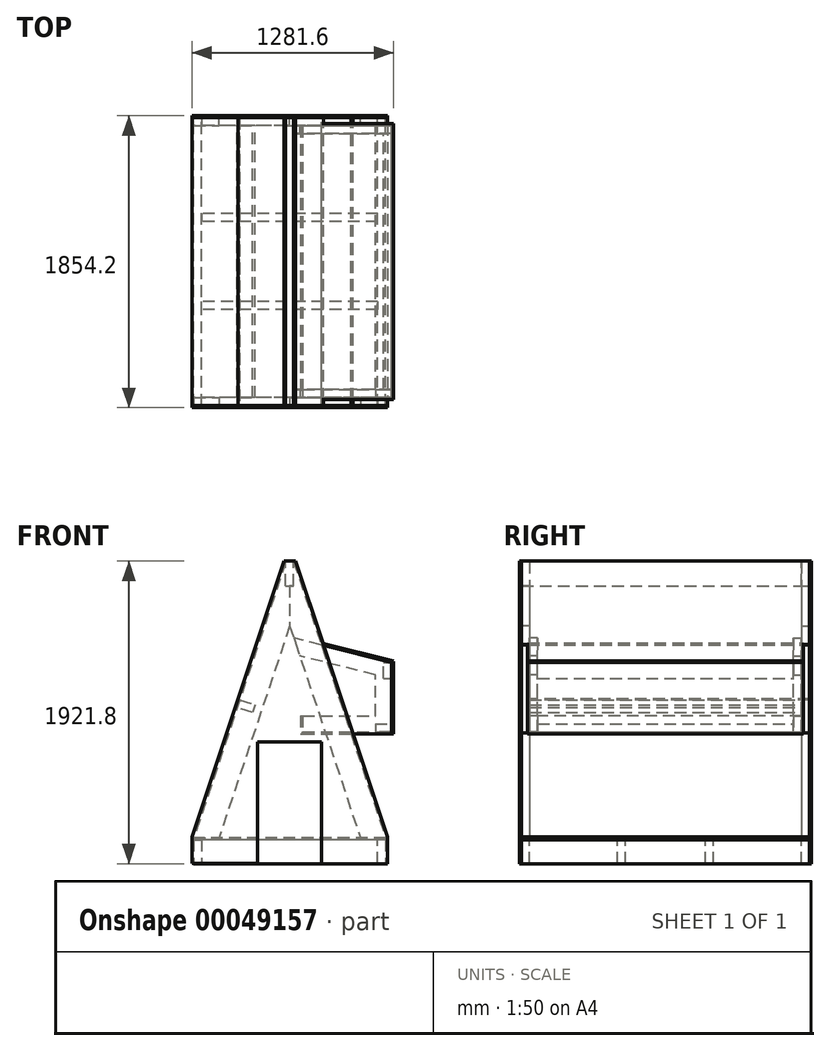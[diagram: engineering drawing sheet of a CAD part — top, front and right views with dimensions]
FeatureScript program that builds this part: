
annotation { "Feature Type Name" : "Feature", "Feature Type Description" : "" }
export const myFeature = defineFeature(function(context is Context, id is Id, definition is map)
    precondition{}
    {
        {
            var Q0;
            Q0=qCreatedBy(makeId("Top.planeOp"),FACE);
            var sketch = newSketch(context, id + "F0", { "sketchPlane" : qUnion([Q0])});
            skLineSegment(sketch, "E0.rect.bottom", {"start": v(609.6, 914.4) * mm, "end": v(-609.6, 914.4) * mm});
            skLineSegment(sketch, "E0.rect.top", {"start": v(609.6, -914.4) * mm, "end": v(-609.6, -914.4) * mm});
            skLineSegment(sketch, "E0.rect.left", {"start": v(609.6, 914.4) * mm, "end": v(609.6, -914.4) * mm});
            skLineSegment(sketch, "E0.rect.right", {"start": v(-609.6, 914.4) * mm, "end": v(-609.6, -914.4) * mm});
            skPoint(sketch, "E0.rect.middle", {"position": v(0, 0) * mm});
            skSolve(sketch);
        }
        {
            var Q0;
            Q0=qCreatedBy(makeId("Front.planeOp"),FACE);
            var sketch = newSketch(context, id + "F1", { "sketchPlane" : qUnion([Q0])});
            skLineSegment(sketch, "E1.bottom", {"start": v(-609.6, 0) * mm, "end": v(-558.8, 0) * mm});
            skLineSegment(sketch, "E1.top", {"start": v(-609.6, -152.4) * mm, "end": v(-558.8, -152.4) * mm});
            skLineSegment(sketch, "E1.left", {"start": v(-609.6, 0) * mm, "end": v(-609.6, -152.4) * mm});
            skLineSegment(sketch, "E1.right", {"start": v(-558.8, 0) * mm, "end": v(-558.8, -152.4) * mm});
            skSolve(sketch);
        }
        {
            var Q0;
            Q0=makeQuery(id+"F1.imprint","IMPRINT",FACE,{"disambiguationData":[TD([[makeQuery(id+"F1.imprint","IMPRINT",EDGE,{"derivedFrom":sQuery(id+"F1.wireOp",EDGE,"E1.bottom")}),-1.0]])]});
            extrude(context, id + "F2", {"entities" : qUnion([Q0]), "depth" : 914.4 * mm, "hasSecondDirection" : true, "secondDirectionOppositeDirection" : true, "secondDirectionDepth" : 914.4 * mm});
        }
        {
            var Q0;
            Q0=makeQuery(id+"F2.opExtrude","SWEPT_BODY",BODY,{"disambiguationData":[OSD([sQuery(id+"F1.wireOp",EDGE,"E1.bottom"),sQuery(id+"F1.wireOp",EDGE,"E1.top"),sQuery(id+"F1.wireOp",EDGE,"E1.left"),sQuery(id+"F1.wireOp",EDGE,"E1.right")])]});
            var Q1;
            Q1=qCreatedBy(makeId("Right.planeOp"),FACE);
            mirror(context, id + "F3", {"entities" : qUnion([Q0]), "mirrorPlane" : qUnion([Q1])});
        }
        {
            var Q0;
            Q0=qCreatedBy(makeId("Right.planeOp"),FACE);
            var sketch = newSketch(context, id + "F4", { "sketchPlane" : qUnion([Q0])});
            skLineSegment(sketch, "E2.bottom", {"start": v(914.4, 0) * mm, "end": v(863.6, 0) * mm});
            skLineSegment(sketch, "E2.top", {"start": v(914.4, -152.4) * mm, "end": v(863.6, -152.4) * mm});
            skLineSegment(sketch, "E2.left", {"start": v(914.4, 0) * mm, "end": v(914.4, -152.4) * mm});
            skLineSegment(sketch, "E2.right", {"start": v(863.6, 0) * mm, "end": v(863.6, -152.4) * mm});
            skSolve(sketch);
        }
        {
            var Q0;
            Q0=makeQuery(id+"F4.imprint","IMPRINT",FACE,{"disambiguationData":[TD([[makeQuery(id+"F4.imprint","IMPRINT",EDGE,{"derivedFrom":sQuery(id+"F4.wireOp",EDGE,"E2.bottom")}),1.0]])]});
            extrude(context, id + "F5", {"entities" : qUnion([Q0]), "endBound" : BoundingType.UP_TO_NEXT, "depth" : 25.4 * mm, "hasSecondDirection" : true, "secondDirectionBound" : SecondDirectionBoundingType.UP_TO_NEXT, "secondDirectionOppositeDirection" : true, "secondDirectionDepth" : 25.4 * mm});
        }
        {
            var Q0;
            Q0=makeQuery(id+"F5.opExtrude","SWEPT_BODY",BODY,{"disambiguationData":[OSD([sQuery(id+"F4.wireOp",EDGE,"E2.bottom"),sQuery(id+"F4.wireOp",EDGE,"E2.top"),sQuery(id+"F4.wireOp",EDGE,"E2.left"),sQuery(id+"F4.wireOp",EDGE,"E2.right")])]});
            var Q1;
            Q1=qCreatedBy(makeId("Front.planeOp"),FACE);
            mirror(context, id + "F6", {"entities" : qUnion([Q0]), "mirrorPlane" : qUnion([Q1])});
        }
        {
            var Q0;
            Q0=qCreatedBy(makeId("Right.planeOp"),FACE);
            var sketch = newSketch(context, id + "F7", { "sketchPlane" : qUnion([Q0])});
            skLineSegment(sketch, "E3.bottom", {"start": v(304.8, 0) * mm, "end": v(254, 0) * mm});
            skLineSegment(sketch, "E3.top", {"start": v(304.8, -152.4) * mm, "end": v(254, -152.4) * mm});
            skLineSegment(sketch, "E3.left", {"start": v(304.8, 0) * mm, "end": v(304.8, -152.4) * mm});
            skLineSegment(sketch, "E3.right", {"start": v(254, 0) * mm, "end": v(254, -152.4) * mm});
            skSolve(sketch);
        }
        {
            var Q0;
            Q0=makeQuery(id+"F7.imprint","IMPRINT",FACE,{"disambiguationData":[TD([[makeQuery(id+"F7.imprint","IMPRINT",EDGE,{"derivedFrom":sQuery(id+"F7.wireOp",EDGE,"E3.bottom")}),1.0]])]});
            extrude(context, id + "F8", {"entities" : qUnion([Q0]), "endBound" : BoundingType.UP_TO_NEXT, "depth" : 25.4 * mm, "hasSecondDirection" : true, "secondDirectionBound" : SecondDirectionBoundingType.UP_TO_NEXT, "secondDirectionOppositeDirection" : true, "secondDirectionDepth" : 25.4 * mm});
        }
        {
            var Q0;
            Q0=makeQuery(id+"F8.opExtrude","SWEPT_BODY",BODY,{"disambiguationData":[OSD([sQuery(id+"F7.wireOp",EDGE,"E3.bottom"),sQuery(id+"F7.wireOp",EDGE,"E3.top"),sQuery(id+"F7.wireOp",EDGE,"E3.left"),sQuery(id+"F7.wireOp",EDGE,"E3.right")])]});
            var Q1;
            Q1=qCreatedBy(makeId("Front.planeOp"),FACE);
            mirror(context, id + "F9", {"entities" : qUnion([Q0]), "mirrorPlane" : qUnion([Q1])});
        }
        {
            var Q0;
            Q0 = qSketchRegion(id + "F0", true);
            extrude(context, id + "F10", {"entities" : qUnion([Q0]), "depth" : 12.7 * mm});
        }
        {
            var Q0;
            Q0=makeQuery(id+"F5.opExtrude","SWEPT_FACE",FACE,{"disambiguationData":[OSD([sQuery(id+"F4.wireOp",EDGE,"E2.left")])]});
            var Q1;
            Q1=makeQuery(id+"F3.opPattern","COPY",VERTEX,{"derivedFrom":makeQuery(id+"F2.opExtrude","CAP_VERTEX",VERTEX,{"disambiguationData":[OSD([sQuery(id+"F1.wireOp",EDGE,"E1.bottom"),sQuery(id+"F1.wireOp",EDGE,"E1.right")])],"isStart":true}),"instanceName":"1"});
            cPlane(context, id + "F11", {"entities" : qUnion([Q0, Q1]), "cplaneType" : CPlaneType.PLANE_POINT, "offset" : 152.4 * mm, "width" : 152.4 * mm, "height" : 152.4 * mm});
        }
        {
            var Q0;
            Q0=qCreatedBy(id+"F11.planeOp",FACE);
            var sketch = newSketch(context, id + "F12", { "sketchPlane" : qUnion([Q0])});
            skLineSegment(sketch, "E4", {"start": v(0, 1841.5) * mm, "end": v(-609.6, 12.7) * mm});
            skLineSegment(sketch, "E5.0", {"start": v(144.58, 1793.3) * mm, "end": v(-465.02, -35.5) * mm});
            skLineSegment(sketch, "E6", {"start": v(0, 1841.5) * mm, "end": v(0, 1170.54) * mm});
            skLineSegment(sketch, "E7", {"start": v(-609.6, 12.7) * mm, "end": v(-200.12, 12.7) * mm});
            skSolve(sketch);
        }
        {
            var Q0;
            {var subQ3=sQuery(id+"F12.wireOp",EDGE,"E4");Q0=makeQuery(id+"F12.imprint","IMPRINT",FACE,{"disambiguationData":[TD([[makeQuery(id+"F12.imprint","IMPRINT",EDGE,{"derivedFrom":subQ3}),1.0]])]});}
            extrude(context, id + "F13", {"entities" : qUnion([Q0]), "oppositeDirection" : true, "depth" : 50.8 * mm});
        }
        {
            var Q0;
            Q0=makeQuery(id+"F13.opExtrude","SWEPT_BODY",BODY,{"disambiguationData":[OSD([sQuery(id+"F12.wireOp",EDGE,"E4"),sQuery(id+"F12.wireOp",EDGE,"E5.0"),sQuery(id+"F12.wireOp",EDGE,"E6"),sQuery(id+"F12.wireOp",EDGE,"E7")])]});
            var Q1;
            Q1=qCreatedBy(makeId("Right.planeOp"),FACE);
            mirror(context, id + "F14", {"entities" : qUnion([Q0]), "mirrorPlane" : qUnion([Q1])});
        }
        {
            var Q0;
            Q0=makeQuery(id+"F14.opPattern","COPY",BODY,{"derivedFrom":makeQuery(id+"F13.opExtrude","SWEPT_BODY",BODY,{"disambiguationData":[OSD([sQuery(id+"F12.wireOp",EDGE,"E4"),sQuery(id+"F12.wireOp",EDGE,"E5.0"),sQuery(id+"F12.wireOp",EDGE,"E6"),sQuery(id+"F12.wireOp",EDGE,"E7")])]}),"instanceName":"1"});
            var Q1;
            Q1=makeQuery(id+"F13.opExtrude","SWEPT_BODY",BODY,{"disambiguationData":[OSD([sQuery(id+"F12.wireOp",EDGE,"E4"),sQuery(id+"F12.wireOp",EDGE,"E5.0"),sQuery(id+"F12.wireOp",EDGE,"E6"),sQuery(id+"F12.wireOp",EDGE,"E7")])]});
            var Q2;
            Q2=qCreatedBy(makeId("Front.planeOp"),FACE);
            mirror(context, id + "F15", {"entities" : qUnion([Q0, Q1]), "mirrorPlane" : qUnion([Q2])});
        }
        {
            var Q0;
            Q0=qCreatedBy(id+"F11.planeOp",FACE);
            var sketch = newSketch(context, id + "F16", { "sketchPlane" : qUnion([Q0])});
            skLineSegment(sketch, "E8.rect.bottom", {"start": v(25.4, 1612.9) * mm, "end": v(-25.4, 1612.9) * mm});
            skLineSegment(sketch, "E8.rect.top", {"start": v(25.4, 2023.26) * mm, "end": v(-25.4, 2023.26) * mm});
            skLineSegment(sketch, "E8.rect.left", {"start": v(25.4, 1612.9) * mm, "end": v(25.4, 2023.26) * mm});
            skLineSegment(sketch, "E8.rect.right", {"start": v(-25.4, 1612.9) * mm, "end": v(-25.4, 2023.26) * mm});
            skPoint(sketch, "E8.rect.middle", {"position": v(0, 1818.08) * mm});
            skLineSegment(sketch, "E9.0", {"start": v(25.4, 1765.3) * mm, "end": v(609.6, 12.7) * mm, "construction": true});
            skPoint(sketch, "E10.orphan", {"position": v(0, 1841.5) * mm});
            skSolve(sketch);
        }
        {
            var Q0;
            Q0=makeQuery(id+"F16.imprint","IMPRINT",FACE,{"disambiguationData":[TD([[makeQuery(id+"F16.imprint","IMPRINT",EDGE,{"derivedFrom":sQuery(id+"F16.wireOp",EDGE,"E8.rect.bottom")}),-1.0]])]});
            extrude(context, id + "F17", {"entities" : qUnion([Q0]), "operationType" : NewBodyOperationType.REMOVE, "endBound" : BoundingType.THROUGH_ALL, "oppositeDirection" : true, "depth" : 25.4 * mm});
        }
        {
            var Q0;
            Q0=makeQuery(id+"F13.opExtrude","CAP_FACE",FACE,{"disambiguationData":[OSD([sQuery(id+"F12.wireOp",EDGE,"E4"),sQuery(id+"F12.wireOp",EDGE,"E5.0"),sQuery(id+"F12.wireOp",EDGE,"E6"),sQuery(id+"F12.wireOp",EDGE,"E7")])],"isStart":true});
            var sketch = newSketch(context, id + "F18", { "sketchPlane" : qUnion([Q0])});
            skLineSegment(sketch, "E11.rect.bottom", {"start": v(-25.4, 1612.9) * mm, "end": v(25.4, 1612.9) * mm});
            skLineSegment(sketch, "E11.rect.top", {"start": v(-25.4, 1765.3) * mm, "end": v(25.4, 1765.3) * mm});
            skLineSegment(sketch, "E11.rect.left", {"start": v(-25.4, 1612.9) * mm, "end": v(-25.4, 1765.3) * mm});
            skLineSegment(sketch, "E11.rect.right", {"start": v(25.4, 1612.9) * mm, "end": v(25.4, 1765.3) * mm});
            skPoint(sketch, "E11.rect.middle", {"position": v(0, 1689.1) * mm});
            skSolve(sketch);
        }
        {
            var Q0;
            Q0=makeQuery(id+"F18.imprint","IMPRINT",FACE,{"disambiguationData":[TD([[makeQuery(id+"F18.imprint","IMPRINT",EDGE,{"derivedFrom":sQuery(id+"F18.wireOp",EDGE,"E11.rect.top")}),-1.0]])]});
            var Q1;
            Q1=makeQuery(id+"F15.opPattern","COPY",FACE,{"derivedFrom":makeQuery(id+"F14.opPattern","COPY",FACE,{"derivedFrom":makeQuery(id+"F13.opExtrude","CAP_FACE",FACE,{"disambiguationData":[OSD([sQuery(id+"F12.wireOp",EDGE,"E4"),sQuery(id+"F12.wireOp",EDGE,"E5.0"),sQuery(id+"F12.wireOp",EDGE,"E6"),sQuery(id+"F12.wireOp",EDGE,"E7")])],"isStart":true}),"instanceName":"1"}),"instanceName":"1"});
            extrude(context, id + "F19", {"entities" : qUnion([Q0]), "endBound" : BoundingType.UP_TO_SURFACE, "oppositeDirection" : true, "endBoundEntityFace" : qUnion([Q1]), "depth" : 25.4 * mm});
        }
        {
            var Q0;
            Q0=makeQuery(id+"F15.opPattern","COPY",FACE,{"derivedFrom":makeQuery(id+"F13.opExtrude","CAP_FACE",FACE,{"disambiguationData":[OSD([sQuery(id+"F12.wireOp",EDGE,"E4"),sQuery(id+"F12.wireOp",EDGE,"E5.0"),sQuery(id+"F12.wireOp",EDGE,"E6"),sQuery(id+"F12.wireOp",EDGE,"E7")])],"isStart":false}),"instanceName":"1"});
            var sketch = newSketch(context, id + "F20", { "sketchPlane" : qUnion([Q0])});
            skLineSegment(sketch, "E12", {"start": v(-224.48, 686.13) * mm, "end": v(-644.91, 686.13) * mm});
            skLineSegment(sketch, "E13", {"start": v(-644.91, 686.13) * mm, "end": v(-644.91, 1126.21) * mm});
            skLineSegment(sketch, "E14", {"start": v(-644.91, 1126.21) * mm, "end": v(-25.96, 1281.68) * mm});
            skLineSegment(sketch, "E15.0", {"start": v(-543.31, 1046.98) * mm, "end": v(-1.21, 1183.14) * mm});
            skLineSegment(sketch, "E15.1", {"start": v(-543.31, 787.73) * mm, "end": v(-543.31, 1046.98) * mm});
            skLineSegment(sketch, "E15.2", {"start": v(-82.13, 787.73) * mm, "end": v(-543.31, 787.73) * mm});
            skLineSegment(sketch, "E16", {"start": v(-25.96, 1281.68) * mm, "end": v(-64.07, 1167.35) * mm});
            skLineSegment(sketch, "E17", {"start": v(-82.13, 787.73) * mm, "end": v(-82.13, 535.6) * mm});
            skLineSegment(sketch, "E18", {"start": v(-224.48, 686.13) * mm, "end": v(-82.13, 686.13) * mm});
            skPoint(sketch, "E18.endSnap0", {"position": v(-82.13, 661.66) * mm});
            skSolve(sketch);
        }
        {
            var Q0;
            {var subQ4=sQuery(id+"F20.wireOp",EDGE,"E13");Q0=makeQuery(id+"F20.imprint","IMPRINT",FACE,{"disambiguationData":[TD([[makeQuery(id+"F20.imprint","IMPRINT",EDGE,{"derivedFrom":subQ4}),-1.0]])]});}
            var Q1;
            {var subQ5=sQuery(id+"F20.wireOp",EDGE,"E16");Q1=makeQuery(id+"F20.imprint","IMPRINT",FACE,{"disambiguationData":[TD([[makeQuery(id+"F20.imprint","IMPRINT",EDGE,{"derivedFrom":subQ5}),-1.0]])]});}
            var Q2;
            {var subQ3=sQuery(id+"F20.wireOp",EDGE,"E12");var subQ5=makeQuery(id+"F15.opPattern","COPY",EDGE,{"derivedFrom":makeQuery(id+"F13.opExtrude","CAP_EDGE",EDGE,{"disambiguationData":[OSD([sQuery(id+"F12.wireOp",EDGE,"E5.0")])],"isStart":false}),"instanceName":"1"});var subQ7=makeQuery(id+"F20.imprint","INTERSECT",VERTEX,{"derivedFrom":[subQ5,subQ3]});Q2=makeQuery(id+"F20.imprint","IMPRINT",FACE,{"disambiguationData":[TD([[makeQuery(id+"F20.imprint","IMPRINT",EDGE,{"disambiguationData":[TD([[subQ7,-1.0]])],"derivedFrom":subQ3}),-1.0]])]});}
            var Q3;
            {var subQ3=sQuery(id+"F20.wireOp",EDGE,"E18");Q3=makeQuery(id+"F20.imprint","IMPRINT",FACE,{"disambiguationData":[TD([[makeQuery(id+"F20.imprint","IMPRINT",EDGE,{"derivedFrom":subQ3}),1.0]])]});}
            extrude(context, id + "F21", {"entities" : qUnion([Q0, Q1, Q2, Q3]), "depth" : 50.8 * mm});
        }
        {
            var Q0;
            Q0=makeQuery(id+"F21.opExtrude","SWEPT_BODY",BODY,{"disambiguationData":[OSD([sQuery(id+"F12.wireOp",EDGE,"E5.0"),sQuery(id+"F20.wireOp",EDGE,"E12"),sQuery(id+"F20.wireOp",EDGE,"E13"),sQuery(id+"F20.wireOp",EDGE,"E14"),sQuery(id+"F20.wireOp",EDGE,"E15.0"),sQuery(id+"F20.wireOp",EDGE,"E15.1"),sQuery(id+"F20.wireOp",EDGE,"E15.2"),sQuery(id+"F20.wireOp",EDGE,"E16")])]});
            var Q1;
            Q1=qCreatedBy(makeId("Front.planeOp"),FACE);
            mirror(context, id + "F22", {"entities" : qUnion([Q0]), "mirrorPlane" : qUnion([Q1])});
        }
        {
            var Q0;
            Q0=makeQuery(id+"F22.opPattern","COPY",FACE,{"derivedFrom":makeQuery(id+"F21.opExtrude","CAP_FACE",FACE,{"disambiguationData":[OSD([sQuery(id+"F12.wireOp",EDGE,"E5.0"),sQuery(id+"F20.wireOp",EDGE,"E12"),sQuery(id+"F20.wireOp",EDGE,"E13"),sQuery(id+"F20.wireOp",EDGE,"E14"),sQuery(id+"F20.wireOp",EDGE,"E15.0"),sQuery(id+"F20.wireOp",EDGE,"E15.1"),sQuery(id+"F20.wireOp",EDGE,"E15.2"),sQuery(id+"F20.wireOp",EDGE,"E16")])],"isStart":false}),"instanceName":"1"});
            var sketch = newSketch(context, id + "F23", { "sketchPlane" : qUnion([Q0])});
            skLineSegment(sketch, "E19.bottom", {"start": v(644.91, 686.13) * mm, "end": v(543.31, 686.13) * mm});
            skLineSegment(sketch, "E19.top", {"start": v(644.91, 736.93) * mm, "end": v(543.31, 736.93) * mm});
            skLineSegment(sketch, "E19.left", {"start": v(644.91, 686.13) * mm, "end": v(644.91, 736.93) * mm});
            skLineSegment(sketch, "E19.right", {"start": v(543.31, 686.13) * mm, "end": v(543.31, 736.93) * mm});
            skSolve(sketch);
        }
        {
            var Q0;
            Q0=makeQuery(id+"F23.imprint","IMPRINT",FACE,{"disambiguationData":[TD([[makeQuery(id+"F23.imprint","IMPRINT",EDGE,{"derivedFrom":sQuery(id+"F23.wireOp",EDGE,"E19.bottom")}),1.0]])]});
            extrude(context, id + "F24", {"entities" : qUnion([Q0]), "endBound" : BoundingType.UP_TO_NEXT, "depth" : 25.4 * mm});
        }
        {
            var Q0;
            Q0=makeQuery(id+"F22.opPattern","COPY",FACE,{"derivedFrom":makeQuery(id+"F21.opExtrude","CAP_FACE",FACE,{"disambiguationData":[OSD([sQuery(id+"F12.wireOp",EDGE,"E5.0"),sQuery(id+"F20.wireOp",EDGE,"E12"),sQuery(id+"F20.wireOp",EDGE,"E13"),sQuery(id+"F20.wireOp",EDGE,"E14"),sQuery(id+"F20.wireOp",EDGE,"E15.0"),sQuery(id+"F20.wireOp",EDGE,"E15.1"),sQuery(id+"F20.wireOp",EDGE,"E15.2"),sQuery(id+"F20.wireOp",EDGE,"E16")])],"isStart":false}),"instanceName":"1"});
            var sketch = newSketch(context, id + "F25", { "sketchPlane" : qUnion([Q0])});
            skLineSegment(sketch, "E20.bottom", {"start": v(644.91, 1126.21) * mm, "end": v(594.11, 1126.21) * mm});
            skLineSegment(sketch, "E20.top", {"start": v(644.91, 1024.61) * mm, "end": v(594.11, 1024.61) * mm});
            skLineSegment(sketch, "E20.left", {"start": v(644.91, 1126.21) * mm, "end": v(644.91, 1024.61) * mm});
            skLineSegment(sketch, "E20.right", {"start": v(594.11, 1126.21) * mm, "end": v(594.11, 1024.61) * mm});
            skSolve(sketch);
        }
        {
            var Q0;
            Q0=makeQuery(id+"F25.imprint","IMPRINT",FACE,{"disambiguationData":[TD([[makeQuery(id+"F25.imprint","IMPRINT",EDGE,{"derivedFrom":sQuery(id+"F25.wireOp",EDGE,"E20.bottom")}),1.0]])]});
            extrude(context, id + "F26", {"entities" : qUnion([Q0]), "endBound" : BoundingType.UP_TO_NEXT, "depth" : 25.4 * mm});
        }
        {
            var Q0;
            Q0=makeQuery(id+"F14.opPattern","COPY",FACE,{"derivedFrom":makeQuery(id+"F13.opExtrude","CAP_FACE",FACE,{"disambiguationData":[OSD([sQuery(id+"F12.wireOp",EDGE,"E4"),sQuery(id+"F12.wireOp",EDGE,"E5.0"),sQuery(id+"F12.wireOp",EDGE,"E6"),sQuery(id+"F12.wireOp",EDGE,"E7")])],"isStart":false}),"instanceName":"1"});
            var sketch = newSketch(context, id + "F27", { "sketchPlane" : qUnion([Q0])});
            skLineSegment(sketch, "E21", {"start": v(-317.5, 889) * mm, "end": v(-221.11, 856.87) * mm});
            skLineSegment(sketch, "E22", {"start": v(-221.11, 856.87) * mm, "end": v(-237.18, 808.68) * mm});
            skLineSegment(sketch, "E23", {"start": v(-237.18, 808.68) * mm, "end": v(-333.56, 840.8) * mm});
            skLineSegment(sketch, "E24", {"start": v(-333.56, 840.8) * mm, "end": v(-317.5, 889) * mm});
            skSolve(sketch);
        }
        {
            var Q0;
            Q0=makeQuery(id+"F27.imprint","IMPRINT",FACE,{"disambiguationData":[TD([[makeQuery(id+"F27.imprint","IMPRINT",EDGE,{"derivedFrom":sQuery(id+"F27.wireOp",EDGE,"E21")}),-1.0]])]});
            extrude(context, id + "F28", {"entities" : qUnion([Q0]), "endBound" : BoundingType.UP_TO_NEXT, "depth" : 25.4 * mm});
        }
        {
            var Q0;
            Q0=makeQuery(id+"F24.opExtrude","SWEPT_FACE",FACE,{"disambiguationData":[OSD([sQuery(id+"F23.wireOp",EDGE,"E19.bottom")])]});
            var sketch = newSketch(context, id + "F29", { "sketchPlane" : qUnion([Q0])});
            skLineSegment(sketch, "E25.0", {"start": v(82.13, 863.6) * mm, "end": v(644.91, 863.6) * mm});
            skLineSegment(sketch, "E26.0", {"start": v(82.13, -863.6) * mm, "end": v(644.91, -863.6) * mm});
            skLineSegment(sketch, "E27", {"start": v(644.91, 863.6) * mm, "end": v(644.91, -863.6) * mm});
            skLineSegment(sketch, "E28", {"start": v(82.13, 863.6) * mm, "end": v(82.13, -863.6) * mm});
            skSolve(sketch);
        }
        {
            var Q0;
            {var subQ4=sQuery(id+"F29.wireOp",EDGE,"E25.0");Q0=makeQuery(id+"F29.imprint","IMPRINT",FACE,{"disambiguationData":[TD([[makeQuery(id+"F29.imprint","IMPRINT",EDGE,{"derivedFrom":subQ4}),-1.0]])]});}
            var Q1;
            {var subQ4=sQuery(id+"F23.wireOp",EDGE,"E19.bottom");var subQ5=makeQuery(id+"F24.opExtrude","CAP_EDGE",EDGE,{"disambiguationData":[OSD([subQ4])],"isStart":true});Q1=makeQuery(id+"F29.imprint","IMPRINT",FACE,{"disambiguationData":[TD([[makeQuery(id+"F29.imprint","IMPRINT",EDGE,{"derivedFrom":subQ5}),1.0]])]});}
            extrude(context, id + "F30", {"entities" : qUnion([Q0, Q1]), "depth" : 12.7 * mm});
        }
        {
            var Q0;
            Q0=makeQuery(id+"F21.opExtrude","CAP_FACE",FACE,{"disambiguationData":[OSD([sQuery(id+"F20.wireOp",EDGE,"E12"),sQuery(id+"F20.wireOp",EDGE,"E13"),sQuery(id+"F20.wireOp",EDGE,"E14"),sQuery(id+"F20.wireOp",EDGE,"E15.0"),sQuery(id+"F20.wireOp",EDGE,"E15.1"),sQuery(id+"F20.wireOp",EDGE,"E15.2"),sQuery(id+"F20.wireOp",EDGE,"E16"),sQuery(id+"F20.wireOp",EDGE,"E17"),sQuery(id+"F20.wireOp",EDGE,"E18")])],"isStart":true});
            var sketch = newSketch(context, id + "F31", { "sketchPlane" : qUnion([Q0])});
            skLineSegment(sketch, "E29.0", {"start": v(644.91, 686.13) * mm, "end": v(644.91, 1126.21) * mm});
            skLineSegment(sketch, "E29.1", {"start": v(644.91, 1126.21) * mm, "end": v(25.96, 1281.68) * mm});
            skLineSegment(sketch, "E29.2", {"start": v(82.13, 673.43) * mm, "end": v(644.91, 673.43) * mm});
            skLineSegment(sketch, "E29.3", {"start": v(25.4, 1765.3) * mm, "end": v(609.6, 12.7) * mm});
            skLineSegment(sketch, "E30", {"start": v(644.91, 673.43) * mm, "end": v(644.91, 686.13) * mm});
            skSolve(sketch);
        }
        {
            var Q0;
            {var subQ3=makeQuery(id+"F21.opExtrude","CAP_EDGE",EDGE,{"disambiguationData":[OSD([sQuery(id+"F20.wireOp",EDGE,"E15.1")])],"isStart":true});Q0=makeQuery(id+"F31.imprint","IMPRINT",FACE,{"disambiguationData":[TD([[makeQuery(id+"F31.imprint","IMPRINT",EDGE,{"derivedFrom":subQ3}),1.0]])]});}
            var Q1;
            {var subQ4=sQuery(id+"F31.wireOp",EDGE,"E29.0");Q1=makeQuery(id+"F31.imprint","IMPRINT",FACE,{"disambiguationData":[TD([[makeQuery(id+"F31.imprint","IMPRINT",EDGE,{"derivedFrom":subQ4}),1.0]])]});}
            var Q2;
            {var subQ3=sQuery(id+"F31.wireOp",EDGE,"E30");Q2=makeQuery(id+"F31.imprint","IMPRINT",FACE,{"disambiguationData":[TD([[makeQuery(id+"F31.imprint","IMPRINT",EDGE,{"derivedFrom":subQ3}),1.0]])]});}
            extrude(context, id + "F32", {"entities" : qUnion([Q0, Q1, Q2]), "depth" : 12.7 * mm});
        }
        {
            var Q0;
            Q0=makeQuery(id+"F32.opExtrude","SWEPT_BODY",BODY,{"disambiguationData":[OSD([sQuery(id+"F31.wireOp",EDGE,"E29.0"),sQuery(id+"F31.wireOp",EDGE,"E29.1"),sQuery(id+"F31.wireOp",EDGE,"E29.2"),sQuery(id+"F31.wireOp",EDGE,"E29.3"),sQuery(id+"F31.wireOp",EDGE,"E30")])]});
            var Q1;
            Q1=qCreatedBy(makeId("Front.planeOp"),FACE);
            mirror(context, id + "F33", {"entities" : qUnion([Q0]), "mirrorPlane" : qUnion([Q1])});
        }
        {
            var Q0;
            Q0=makeQuery(id+"F26.opExtrude","SWEPT_FACE",FACE,{"disambiguationData":[OSD([sQuery(id+"F25.wireOp",EDGE,"E20.left")])]});
            var sketch = newSketch(context, id + "F34", { "sketchPlane" : qUnion([Q0])});
            skLineSegment(sketch, "E31.0", {"start": v(-876.3, 673.43) * mm, "end": v(-876.3, 1126.21) * mm});
            skLineSegment(sketch, "E31.1", {"start": v(876.3, 673.43) * mm, "end": v(876.3, 1126.21) * mm});
            skLineSegment(sketch, "E32", {"start": v(876.3, 1126.21) * mm, "end": v(-876.3, 1126.21) * mm});
            skLineSegment(sketch, "E33", {"start": v(-876.3, 673.43) * mm, "end": v(876.3, 673.43) * mm});
            skSolve(sketch);
        }
        {
            var Q0;
            {var subQ4=sQuery(id+"F34.wireOp",EDGE,"E31.0");Q0=makeQuery(id+"F34.imprint","IMPRINT",FACE,{"disambiguationData":[TD([[makeQuery(id+"F34.imprint","IMPRINT",EDGE,{"derivedFrom":subQ4}),-1.0]])]});}
            var Q1;
            {var subQ1=sQuery(id+"F20.wireOp",EDGE,"E13");var subQ2=makeQuery(id+"F26.opExtrude","CAP_EDGE",EDGE,{"disambiguationData":[OSD([subQ1])],"isStart":false});Q1=makeQuery(id+"F34.imprint","IMPRINT",FACE,{"disambiguationData":[TD([[makeQuery(id+"F34.imprint","IMPRINT",EDGE,{"derivedFrom":subQ2}),1.0]])]});}
            extrude(context, id + "F35", {"entities" : qUnion([Q0, Q1]), "depth" : 12.7 * mm});
        }
        {
            var Q0;
            Q0=makeQuery(id+"F15.opPattern","COPY",FACE,{"derivedFrom":makeQuery(id+"F13.opExtrude","SWEPT_FACE",FACE,{"disambiguationData":[OSD([sQuery(id+"F12.wireOp",EDGE,"E4")])]}),"instanceName":"1"});
            var sketch = newSketch(context, id + "F36", { "sketchPlane" : qUnion([Q0])});
            skLineSegment(sketch, "E34.0", {"start": v(-914.4, 1666.68) * mm, "end": v(-914.4, -180.72) * mm});
            skLineSegment(sketch, "E35.1", {"start": v(914.4, 1666.68) * mm, "end": v(914.4, -180.72) * mm});
            skLineSegment(sketch, "E36", {"start": v(-914.4, 1110.48) * mm, "end": v(914.4, 1110.48) * mm});
            skLineSegment(sketch, "E37", {"start": v(914.4, 1666.68) * mm, "end": v(-914.4, 1666.68) * mm});
            skLineSegment(sketch, "E38.0", {"start": v(914.4, -180.72) * mm, "end": v(-914.4, -180.72) * mm});
            skLineSegment(sketch, "E39", {"start": v(-914.4, 515.75) * mm, "end": v(914.4, 515.75) * mm});
            skSolve(sketch);
        }
        {
            var Q0;
            {var subQ0=sQuery(id+"F36.wireOp",EDGE,"E37");var subQ1=sQuery(id+"F36.wireOp",EDGE,"E35.1");var subQ2=makeQuery(id+"F36.imprint","INTERSECT",VERTEX,{"derivedFrom":[subQ1,subQ0]});Q0=makeQuery(id+"F36.imprint","IMPRINT",FACE,{"disambiguationData":[TD([[makeQuery(id+"F36.imprint","IMPRINT",EDGE,{"disambiguationData":[TD([[subQ2,-1.0]])],"derivedFrom":subQ1}),-1.0]])]});}
            var Q1;
            {var subQ3=sQuery(id+"F36.wireOp",EDGE,"E37");var subQ5=sQuery(id+"F36.wireOp",EDGE,"E34.0");var subQ6=makeQuery(id+"F36.imprint","INTERSECT",VERTEX,{"derivedFrom":[subQ5,subQ3]});Q1=makeQuery(id+"F36.imprint","IMPRINT",FACE,{"disambiguationData":[TD([[makeQuery(id+"F36.imprint","IMPRINT",EDGE,{"disambiguationData":[TD([[subQ6,-1.0]])],"derivedFrom":subQ5}),1.0]])]});}
            extrude(context, id + "F37", {"entities" : qUnion([Q0, Q1]), "depth" : 12.95 * mm});
        }
        {
            var Q0;
            {var subQ3=sQuery(id+"F36.wireOp",EDGE,"E38.0");var subQ5=sQuery(id+"F36.wireOp",EDGE,"E35.1");var subQ6=makeQuery(id+"F36.imprint","INTERSECT",VERTEX,{"derivedFrom":[subQ5,subQ3]});Q0=makeQuery(id+"F36.imprint","IMPRINT",FACE,{"disambiguationData":[TD([[makeQuery(id+"F36.imprint","IMPRINT",EDGE,{"disambiguationData":[TD([[subQ6,1.0]])],"derivedFrom":subQ5}),-1.0]])]});}
            var Q1;
            {var subQ3=sQuery(id+"F36.wireOp",EDGE,"E34.0");var subQ5=sQuery(id+"F36.wireOp",EDGE,"E38.0");var subQ7=makeQuery(id+"F36.imprint","INTERSECT",VERTEX,{"derivedFrom":[subQ3,subQ5]});Q1=makeQuery(id+"F36.imprint","IMPRINT",FACE,{"disambiguationData":[TD([[makeQuery(id+"F36.imprint","IMPRINT",EDGE,{"disambiguationData":[TD([[subQ7,1.0]])],"derivedFrom":subQ3}),1.0]])]});}
            extrude(context, id + "F38", {"entities" : qUnion([Q0, Q1]), "depth" : 12.7 * mm});
        }
        {
            var Q0;
            Q0=makeQuery(id+"F14.opPattern","COPY",FACE,{"derivedFrom":makeQuery(id+"F13.opExtrude","SWEPT_FACE",FACE,{"disambiguationData":[OSD([sQuery(id+"F12.wireOp",EDGE,"E4")])]}),"instanceName":"1"});
            var sketch = newSketch(context, id + "F39", { "sketchPlane" : qUnion([Q0])});
            skLineSegment(sketch, "E40.0", {"start": v(-914.4, 1666.68) * mm, "end": v(-914.4, -180.72) * mm});
            skLineSegment(sketch, "E40.1", {"start": v(914.4, 1666.68) * mm, "end": v(914.4, -180.72) * mm});
            skLineSegment(sketch, "E41", {"start": v(-914.4, 742.98) * mm, "end": v(914.4, 742.98) * mm});
            skLineSegment(sketch, "E42", {"start": v(-914.4, 1666.68) * mm, "end": v(914.4, 1666.68) * mm});
            skLineSegment(sketch, "E43", {"start": v(-914.4, -180.72) * mm, "end": v(914.4, -180.72) * mm});
            skSolve(sketch);
        }
        {
            var Q0;
            {var subQ3=sQuery(id+"F39.wireOp",EDGE,"E42");var subQ5=sQuery(id+"F39.wireOp",EDGE,"E40.1");var subQ6=makeQuery(id+"F39.imprint","INTERSECT",VERTEX,{"derivedFrom":[subQ5,subQ3]});Q0=makeQuery(id+"F39.imprint","IMPRINT",FACE,{"disambiguationData":[TD([[makeQuery(id+"F39.imprint","IMPRINT",EDGE,{"disambiguationData":[TD([[subQ6,-1.0]])],"derivedFrom":subQ5}),-1.0]])]});}
            var Q1;
            {var subQ3=sQuery(id+"F39.wireOp",EDGE,"E42");var subQ5=sQuery(id+"F39.wireOp",EDGE,"E40.0");var subQ6=makeQuery(id+"F39.imprint","INTERSECT",VERTEX,{"derivedFrom":[subQ5,subQ3]});Q1=makeQuery(id+"F39.imprint","IMPRINT",FACE,{"disambiguationData":[TD([[makeQuery(id+"F39.imprint","IMPRINT",EDGE,{"disambiguationData":[TD([[subQ6,-1.0]])],"derivedFrom":subQ5}),1.0]])]});}
            extrude(context, id + "F40", {"entities" : qUnion([Q0, Q1]), "depth" : 12.7 * mm});
        }
        {
            var Q0;
            {var subQ3=sQuery(id+"F39.wireOp",EDGE,"E43");var subQ5=sQuery(id+"F39.wireOp",EDGE,"E40.1");var subQ6=makeQuery(id+"F39.imprint","INTERSECT",VERTEX,{"derivedFrom":[subQ5,subQ3]});Q0=makeQuery(id+"F39.imprint","IMPRINT",FACE,{"disambiguationData":[TD([[makeQuery(id+"F39.imprint","IMPRINT",EDGE,{"disambiguationData":[TD([[subQ6,1.0]])],"derivedFrom":subQ5}),-1.0]])]});}
            var Q1;
            {var subQ3=sQuery(id+"F39.wireOp",EDGE,"E43");var subQ5=sQuery(id+"F39.wireOp",EDGE,"E40.0");var subQ6=makeQuery(id+"F39.imprint","INTERSECT",VERTEX,{"derivedFrom":[subQ5,subQ3]});Q1=makeQuery(id+"F39.imprint","IMPRINT",FACE,{"disambiguationData":[TD([[makeQuery(id+"F39.imprint","IMPRINT",EDGE,{"disambiguationData":[TD([[subQ6,1.0]])],"derivedFrom":subQ5}),1.0]])]});}
            extrude(context, id + "F41", {"entities" : qUnion([Q0, Q1]), "depth" : 12.7 * mm});
        }
        {
            var Q0;
            Q0=makeQuery(id+"F22.opPattern","COPY",FACE,{"derivedFrom":makeQuery(id+"F21.opExtrude","SWEPT_FACE",FACE,{"disambiguationData":[OSD([sQuery(id+"F20.wireOp",EDGE,"E17")])]}),"instanceName":"1"});
            var sketch = newSketch(context, id + "F42", { "sketchPlane" : qUnion([Q0])});
            skLineSegment(sketch, "E44.0", {"start": v(863.6, 673.43) * mm, "end": v(-863.6, 673.43) * mm});
            skLineSegment(sketch, "E45", {"start": v(-863.6, 787.73) * mm, "end": v(-863.6, 673.43) * mm});
            skLineSegment(sketch, "E46", {"start": v(-863.6, 787.73) * mm, "end": v(890.66, 787.73) * mm});
            skLineSegment(sketch, "E47", {"start": v(863.6, 673.43) * mm, "end": v(863.6, 787.73) * mm});
            skSolve(sketch);
        }
        {
            var Q0;
            {var subQ3=sQuery(id+"F42.wireOp",EDGE,"E44.0");Q0=makeQuery(id+"F42.imprint","IMPRINT",FACE,{"disambiguationData":[TD([[makeQuery(id+"F42.imprint","IMPRINT",EDGE,{"derivedFrom":subQ3}),-1.0]])]});}
            var Q1;
            {var subQ0=sQuery(id+"F20.wireOp",EDGE,"E17");var subQ1=makeQuery(id+"F22.opPattern","COPY",EDGE,{"derivedFrom":makeQuery(id+"F21.opExtrude","CAP_EDGE",EDGE,{"disambiguationData":[OSD([subQ0])],"isStart":false}),"instanceName":"1"});Q1=makeQuery(id+"F42.imprint","IMPRINT",FACE,{"disambiguationData":[TD([[makeQuery(id+"F42.imprint","IMPRINT",EDGE,{"derivedFrom":subQ1}),-1.0]])]});}
            extrude(context, id + "F43", {"entities" : qUnion([Q0, Q1]), "depth" : 12.7 * mm});
        }
        {
            var Q0;
            Q0=makeQuery(id+"F21.opExtrude","SWEPT_FACE",FACE,{"disambiguationData":[OSD([sQuery(id+"F20.wireOp",EDGE,"E14")])]});
            var sketch = newSketch(context, id + "F44", { "sketchPlane" : qUnion([Q0])});
            skLineSegment(sketch, "E48.0", {"start": v(-106.29, -914.4) * mm, "end": v(-106.29, 914.4) * mm});
            skLineSegment(sketch, "E48.1", {"start": v(363.44, 876.3) * mm, "end": v(363.44, -876.3) * mm});
            skLineSegment(sketch, "E49", {"start": v(363.44, -876.3) * mm, "end": v(-106.29, -876.3) * mm});
            skLineSegment(sketch, "E50", {"start": v(363.44, 876.3) * mm, "end": v(-106.29, 876.3) * mm});
            skSolve(sketch);
        }
        {
            var Q0;
            Q0=makeQuery(id+"F5.opExtrude","SWEPT_FACE",FACE,{"disambiguationData":[OSD([sQuery(id+"F4.wireOp",EDGE,"E2.left")])]});
            var sketch = newSketch(context, id + "F45", { "sketchPlane" : qUnion([Q0])});
            skPoint(sketch, "E51.0", {"position": v(37.45, 1769.32) * mm});
            skPoint(sketch, "E52.1", {"position": v(621.65, 16.72) * mm});
            skLineSegment(sketch, "E53", {"start": v(37.45, 1769.32) * mm, "end": v(621.65, 16.72) * mm});
            skLineSegment(sketch, "E54", {"start": v(621.65, 16.72) * mm, "end": v(621.65, -151.25) * mm});
            skLineSegment(sketch, "E55", {"start": v(621.65, -151.25) * mm, "end": v(-638.79, -152.4) * mm});
            skLineSegment(sketch, "E56", {"start": v(0, -260.28) * mm, "end": v(0, 1987.22) * mm, "construction": true});
            skLineSegment(sketch, "E57.MirrorCS", {"start": v(-37.45, 1769.32) * mm, "end": v(-621.65, 16.72) * mm});
            skLineSegment(sketch, "E58", {"start": v(-37.45, 1769.32) * mm, "end": v(37.45, 1769.32) * mm});
            skLineSegment(sketch, "E59", {"start": v(-621.65, 16.72) * mm, "end": v(-621.48, -166.5) * mm});
            skSolve(sketch);
        }
        {
            var Q0;
            Q0=makeQuery(id+"F45.imprint","IMPRINT",FACE,{"disambiguationData":[TD([[makeQuery(id+"F45.imprint","IMPRINT",EDGE,{"derivedFrom":sQuery(id+"F45.wireOp",EDGE,"E53")}),-1.0]])]});
            var Q1;
            {var subQ2=sQuery(id+"F1.wireOp",EDGE,"E1.right");var subQ8=makeQuery(id+"F5.opExtrude","SWEPT_EDGE",EDGE,{"disambiguationData":[OSD([sQuery(id+"F1.wireOp",EDGE,"E1.bottom"),subQ2])]});Q1=makeQuery(id+"F45.imprint","IMPRINT",FACE,{"disambiguationData":[TD([[makeQuery(id+"F45.imprint","IMPRINT",EDGE,{"derivedFrom":subQ8}),-1.0]])]});}
            extrude(context, id + "F46", {"entities" : qUnion([Q0, Q1]), "depth" : 12.7 * mm});
        }
        {
            var Q0;
            Q0=makeQuery(id+"F15.opPattern","COPY",FACE,{"derivedFrom":makeQuery(id+"F14.opPattern","COPY",FACE,{"derivedFrom":makeQuery(id+"F13.opExtrude","CAP_FACE",FACE,{"disambiguationData":[OSD([sQuery(id+"F12.wireOp",EDGE,"E4"),sQuery(id+"F12.wireOp",EDGE,"E5.0"),sQuery(id+"F12.wireOp",EDGE,"E6"),sQuery(id+"F12.wireOp",EDGE,"E7")])],"isStart":true}),"instanceName":"1"}),"instanceName":"1"});
            var sketch = newSketch(context, id + "F47", { "sketchPlane" : qUnion([Q0])});
            skPoint(sketch, "E60.0", {"position": v(-37.45, 1769.32) * mm});
            skPoint(sketch, "E60.1", {"position": v(-37.45, 1769.32) * mm});
            skPoint(sketch, "E60.2", {"position": v(-621.65, 16.72) * mm});
            skLineSegment(sketch, "E60.3", {"start": v(-37.45, 1769.32) * mm, "end": v(-621.65, 16.72) * mm});
            skLineSegment(sketch, "E60.4", {"start": v(-621.65, 16.72) * mm, "end": v(-621.65, -151.25) * mm});
            skLineSegment(sketch, "E60.5", {"start": v(-621.65, -151.25) * mm, "end": v(638.79, -152.4) * mm});
            skLineSegment(sketch, "E60.6", {"start": v(0, -260.28) * mm, "end": v(0, 1987.22) * mm, "construction": true});
            skLineSegment(sketch, "E60.7", {"start": v(37.45, 1769.32) * mm, "end": v(621.65, 16.72) * mm});
            skLineSegment(sketch, "E60.8", {"start": v(37.45, 1769.32) * mm, "end": v(-37.45, 1769.32) * mm});
            skLineSegment(sketch, "E60.9", {"start": v(621.65, 16.72) * mm, "end": v(621.48, -166.5) * mm});
            skLineSegment(sketch, "E61.rect.bottom", {"start": v(203.2, 622.3) * mm, "end": v(-203.2, 622.3) * mm});
            skLineSegment(sketch, "E61.rect.top", {"start": v(203.2, -152) * mm, "end": v(-203.2, -152) * mm});
            skLineSegment(sketch, "E61.rect.left", {"start": v(203.2, 622.3) * mm, "end": v(203.2, -152) * mm});
            skLineSegment(sketch, "E61.rect.right", {"start": v(-203.2, 622.3) * mm, "end": v(-203.2, -152) * mm});
            skPoint(sketch, "E61.rect.middle", {"position": v(0, 235.15) * mm});
            skSolve(sketch);
        }
        {
            var Q0;
            Q0=makeQuery(id+"F47.imprint","IMPRINT",FACE,{"disambiguationData":[TD([[makeQuery(id+"F47.imprint","IMPRINT",EDGE,{"derivedFrom":sQuery(id+"F47.wireOp",EDGE,"E60.3")}),1.0]])]});
            var Q1;
            {var subQ1=sQuery(id+"F12.wireOp",EDGE,"E5.0");Q1=makeQuery(id+"F47.imprint","IMPRINT",FACE,{"disambiguationData":[TD([[makeQuery(id+"F47.imprint","IMPRINT",EDGE,{"derivedFrom":makeQuery(id+"F15.opPattern","COPY",EDGE,{"derivedFrom":makeQuery(id+"F14.opPattern","COPY",EDGE,{"derivedFrom":makeQuery(id+"F13.opExtrude","CAP_EDGE",EDGE,{"disambiguationData":[OSD([subQ1])],"isStart":true}),"instanceName":"1"}),"instanceName":"1"})}),-1.0]])]});}
            extrude(context, id + "F48", {"entities" : qUnion([Q0, Q1]), "depth" : 12.7 * mm});
        }
        {
            var Q0;
            {var subQ3=sQuery(id+"F47.wireOp",EDGE,"E61.rect.bottom");Q0=makeQuery(id+"F47.imprint","IMPRINT",FACE,{"disambiguationData":[TD([[makeQuery(id+"F47.imprint","IMPRINT",EDGE,{"derivedFrom":subQ3}),1.0]])]});}
            extrude(context, id + "F49", {"entities" : qUnion([Q0]), "depth" : 12.7 * mm});
        }
        {
            var Q0;
            Q0=makeQuery(id+"F44.imprint","IMPRINT",FACE,{"disambiguationData":[TD([[makeQuery(id+"F44.imprint","IMPRINT",EDGE,{"derivedFrom":sQuery(id+"F44.wireOp",EDGE,"E48.1")}),-1.0]])]});
            var Q1;
            {var subQ0=sQuery(id+"F20.wireOp",EDGE,"E14");var subQ4=makeQuery(id+"F21.opExtrude","SWEPT_EDGE",EDGE,{"disambiguationData":[OSD([sQuery(id+"F20.wireOp",EDGE,"E13"),subQ0])]});Q1=makeQuery(id+"F44.imprint","IMPRINT",FACE,{"disambiguationData":[TD([[makeQuery(id+"F44.imprint","IMPRINT",EDGE,{"derivedFrom":subQ4}),-1.0]])]});}
            extrude(context, id + "F50", {"entities" : qUnion([Q0, Q1]), "depth" : 12.7 * mm});
        }
    });
